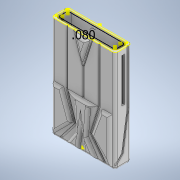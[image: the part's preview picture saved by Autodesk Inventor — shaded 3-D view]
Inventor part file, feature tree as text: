
AUTODESK INVENTOR PART (.ipt)
format: ipt  version: 2022 (Build 260153000, 153)  size: 473,600 bytes
history: native  units: in
note: dims shown in document units (in); Inventor stores cm internally (conversion verified against a paired STEP export)
features: sketch x15, projected_geometry x14, extrude x13, fillet x6, mirror x2, plane x1
ambient origin geometry x8: Origin, YZ Plane, XZ Plane, XY Plane, X Axis, Y Axis, Z Axis, Center Point
bodies: Solid1 (feature_tree)
feature tree (51):
  extrude  "Extrusion1"  Depth=1.875in
  extrude  "Extrusion2"  Depth=0.125in
  fillet  "Fillet1"  Radius=2.0in
  extrude  "Extrusion3"  Depth=0.125in
  fillet  "Fillet2"  Radius=0.4in
  sketch  "Sketch4"  dims[d10=1.0in d11=0.25in d12=0.0in d13=0.125in]
  extrude  "Extrusion4"  Depth=0.25in TaperAngle=0.0deg
  fillet  "Fillet4"  Radius=0.125in
  extrude  "Extrusion6"  Depth=0.125in
  fillet  "Fillet5"  Radius=0.125in
  extrude  "Extrusion7"  Depth=0.0394in TaperAngle=0.0deg
  mirror  "Mirror1"
  extrude  "Extrusion8"  Depth=0.0787in
  fillet  "Fillet6"  Radius=0.0394in
  mirror  "Mirror2"
  sketch  "Sketch7"  dims[d27=0.55in d28=0.0787in d29=0.0394in d30=0.0in]
  plane  "Work Plane1"
  extrude  "Extrusion9"  Depth=0.125in TaperAngle=0.0deg
  extrude  "Extrusion10"  Depth=2.5in
  extrude  "Extrusion11"  Depth=1.0in
  extrude  "Extrusion12"  Depth=2.0in
  extrude  "Extrusion13"  Depth=0.125in TaperAngle=0.0deg
  extrude  "Extrusion15"  Depth=0.0415in
  fillet  "Fillet7"  Radius=0.0415in
  sketch  "Sketch15"  dims[d48=0.0415in]
  sketch  "Sketch16"  dims[d50=0.0415in d51=1.0in d52=0.0in d55=0.06in d56=0.125in d57=0.0in d58=0.125in d59=0.08in]
  sketch  "Sketch1"  dims[d0=2.475in d1=1.875in]
  sketch  "Sketch2"  dims[d2=0.75in d3=0.0in d4=0.125in d5=2.0in d6=0.0in]
  projected_geometry  "Projected Loop1"
  sketch  "Sketch3"  dims[d7=0.125in d8=0.12in d9=0.4in]
  projected_geometry  "Projected Loop2"
  sketch  "Sketch5"  dims[d14=0.125in d15=0.0in d19=0.125in d20=0.125in d21=0.0in]
  projected_geometry  "Projected Loop3"
  projected_geometry  "Projected Loop4"
  sketch  "Sketch6"  dims[d22=0.125in d25=0.0394in d26=0.0in]
  projected_geometry  "Projected Loop5"
  projected_geometry  "Projected Loop6"
  projected_geometry  "Projected Loop7"
  projected_geometry  "Projected Loop8"
  projected_geometry  "Projected Loop9"
  projected_geometry  "Projected Loop10"
  sketch  "Sketch8"  dims[d31=0.125in d32=0.125in d33=0.0in]
  sketch  "Sketch9"  dims[d34=2.5in d35=0.0in d36=0.375in]
  projected_geometry  "Projected Loop11"
  sketch  "Sketch10"  dims[d37=1.25in d38=1.0in]
  sketch  "Sketch11"  dims[d39=0.0625in d40=2.0in]
  projected_geometry  "Projected Loop12"
  sketch  "Sketch12"  dims[d41=0.125in d42=10.0in d43=0.0in]
  sketch  "Sketch14"  dims[d44=10.0in d45=0.0in d46=0.4in d47=0.0415in]
  projected_geometry  "Projected Loop14"
  projected_geometry  "Projected Loop15"
